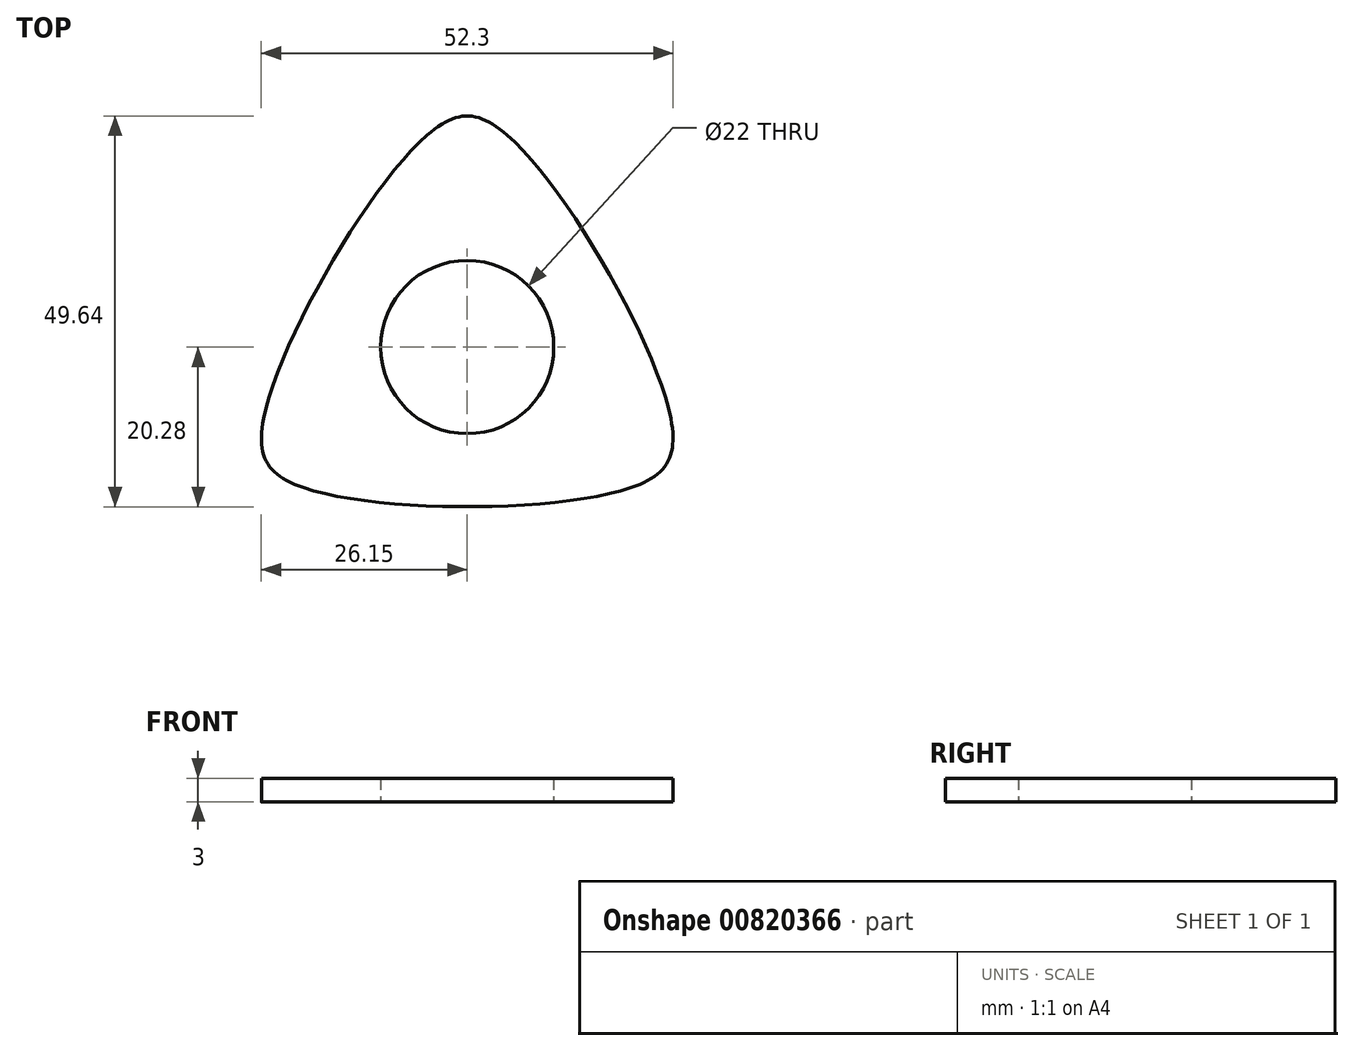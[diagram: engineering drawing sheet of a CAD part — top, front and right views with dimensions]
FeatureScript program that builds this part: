
annotation { "Feature Type Name" : "Feature", "Feature Type Description" : "" }
export const myFeature = defineFeature(function(context is Context, id is Id, definition is map)
    precondition{}
    {
        {
            var Q0;
            Q0=qCreatedBy(makeId("Top.planeOp"),FACE);
            var sketch = newSketch(context, id + "F0", { "sketchPlane" : qUnion([Q0])});
            skCircle(sketch, "E0", {"center": v(0, 0) * mm, "radius": 11 * mm});
            skArc(sketch, "E1", {"start": v(-4.02, 14.45) * mm, "mid": v(-13, 7.5) * mm, "end": v(-14.52, -3.75) * mm});
            skCircle(sketch, "E2", {"center": v(0, 41.06) * mm, "radius": 11 * mm});
            skArc(sketch, "E3", {"start": v(5.07, 26.94) * mm, "mid": v(0, 56.06) * mm, "end": v(-5.07, 26.94) * mm});
            skArc(sketch, "E4.1.0", {"start": v(-25.87, -9.08) * mm, "mid": v(-48.55, -28.03) * mm, "end": v(-20.8, -17.86) * mm});
            skCircle(sketch, "E4.1.1", {"center": v(-35.56, -20.53) * mm, "radius": 11 * mm});
            skArc(sketch, "E4.2.0", {"start": v(20.8, -17.86) * mm, "mid": v(48.55, -28.03) * mm, "end": v(25.87, -9.08) * mm});
            skCircle(sketch, "E4.2.1", {"center": v(35.56, -20.53) * mm, "radius": 11 * mm});
            skArc(sketch, "E5.trimOffspring", {"start": v(-10.5, -10.7) * mm, "mid": v(0, -15) * mm, "end": v(10.5, -10.7) * mm});
            skArc(sketch, "E6.trimOffspring", {"start": v(14.52, -3.75) * mm, "mid": v(13, 7.5) * mm, "end": v(4.02, 14.45) * mm});
            skPoint(sketch, "E7.center.orphan", {"position": v(0, 21.08) * mm});
            skFitSpline(sketch, "E8", {"points": [v(-5.07, 26.94) * mm, v(-25.87, -9.08) * mm, v(-20.8, -17.86) * mm, v(20.8, -17.86) * mm, v(25.87, -9.08) * mm, v(5.07, 26.94) * mm, v(-5.07, 26.94) * mm]});
            skSolve(sketch);
        }
        {
            var Q0;
            Q0=makeQuery(id+"F0.imprint","IMPRINT",FACE,{"disambiguationData":[TD([[makeQuery(id+"F0.imprint","IMPRINT",EDGE,{"derivedFrom":sQuery(id+"F0.wireOp",EDGE,"E0")}),-1.0]])]});
            extrude(context, id + "F1", {"entities" : qUnion([Q0]), "depth" : 3 * mm, "offsetDistance" : 25 * mm});
        }
    });
